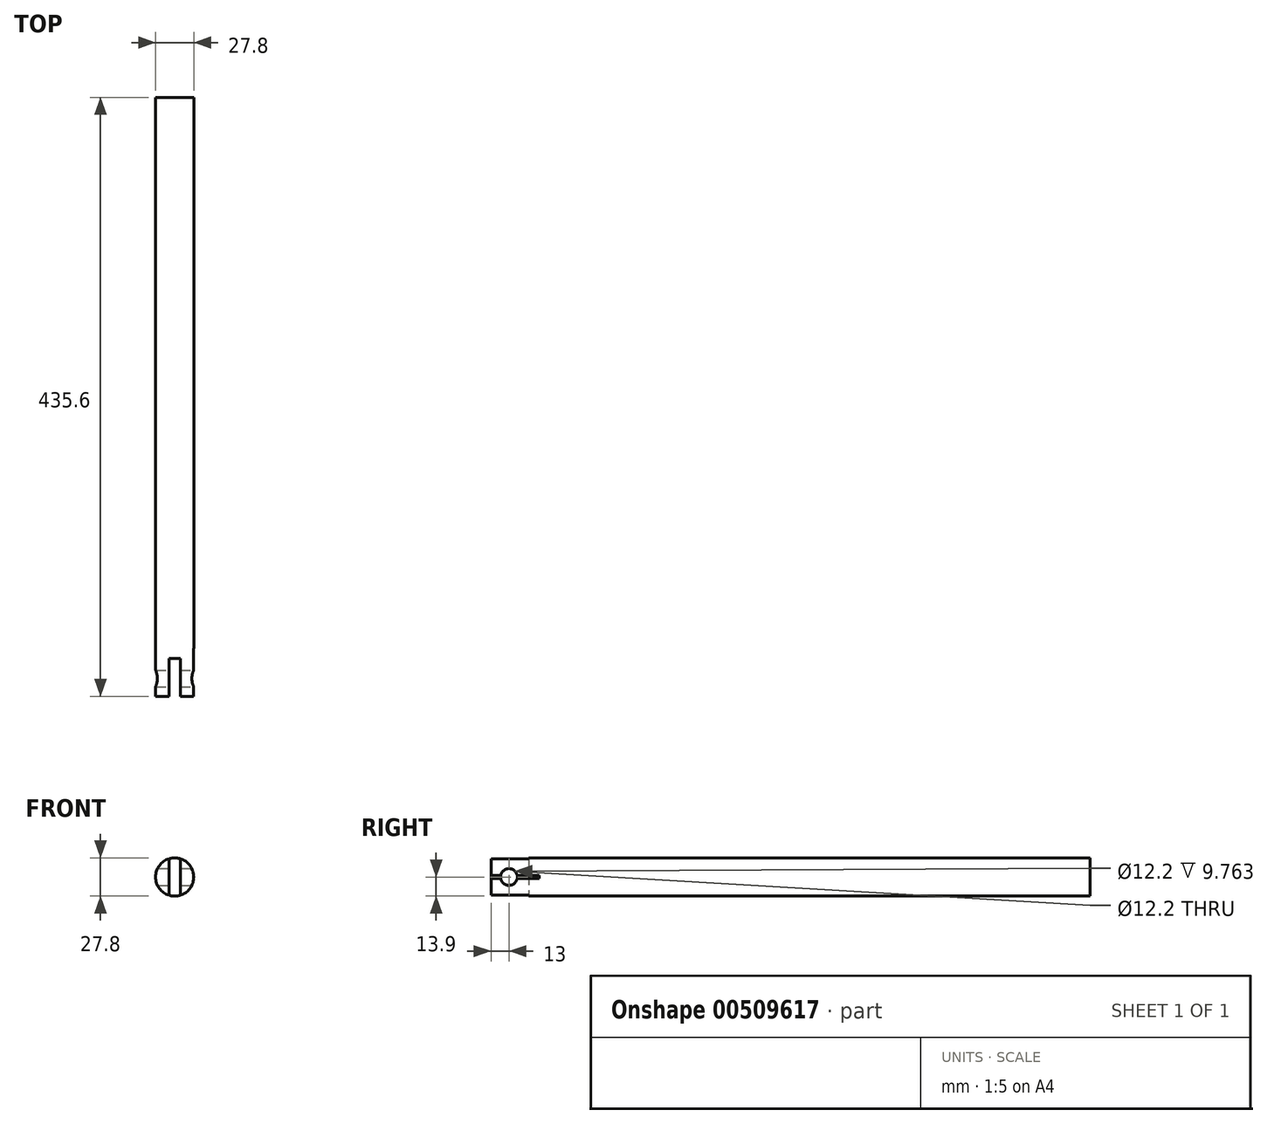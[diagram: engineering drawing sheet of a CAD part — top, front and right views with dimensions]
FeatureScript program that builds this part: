
annotation { "Feature Type Name" : "Feature", "Feature Type Description" : "" }
export const myFeature = defineFeature(function(context is Context, id is Id, definition is map)
    precondition{}
    {
        {
            var Q0;
            Q0=qCreatedBy(makeId("Front.planeOp"),FACE);
            var sketch = newSketch(context, id + "F0", { "sketchPlane" : qUnion([Q0])});
            skCircle(sketch, "E0", {"center": v(0, 0) * mm, "radius": 13.9 * mm});
            skSolve(sketch);
        }
        {
            var Q0;
            Q0=qSketchRegion(id+"F0",true);
            extrude(context, id + "F1", {"entities" : qUnion([Q0]), "endBound" : BoundingType.SYMMETRIC, "depth" : 435.6 * mm});
        }
        {
            var Q0;
            Q0=makeQuery(id+"F1.opExtrude","CAP_FACE",FACE,{"disambiguationData":[OSD([sQuery(id+"F0.wireOp",EDGE,"E0")])],"isStart":false});
            var sketch = newSketch(context, id + "F2", { "sketchPlane" : qUnion([Q0])});
            skLineSegment(sketch, "E1.left", {"start": v(-13.86, 1.02) * mm, "end": v(-13.86, -1.02) * mm});
            skLineSegment(sketch, "E1.right", {"start": v(13.86, 1.02) * mm, "end": v(13.86, -1.02) * mm});
            skPoint(sketch, "E1.middle", {"position": v(0, 0) * mm});
            skSolve(sketch);
        }
        {
            var Q0;
            {var subQ0=sQuery(id+"F2.wireOp",EDGE,"E1.right");Q0=makeQuery(id+"F2.imprint","IMPRINT",FACE,{"disambiguationData":[TD([[makeQuery(id+"F2.imprint","IMPRINT",EDGE,{"derivedFrom":subQ0}),1.0]])]});}
            extrude(context, id + "F3", {"entities" : qUnion([Q0]), "operationType" : NewBodyOperationType.REMOVE, "oppositeDirection" : true, "depth" : 35 * mm});
        }
        {
            var Q0;
            Q0=makeQuery(id+"F3.boolean.opBoolean","COPY",FACE,{"derivedFrom":makeQuery(id+"F3.opExtrude","SWEPT_FACE",FACE,{"disambiguationData":[OSD([sQuery(id+"F2.wireOp",EDGE,"E1.right")])]})});
            var sketch = newSketch(context, id + "F4", { "sketchPlane" : qUnion([Q0])});
            skLineSegment(sketch, "E2", {"start": v(-204.8, 0) * mm, "end": v(-217.8, 0) * mm});
            skPoint(sketch, "E2.startSnap0", {"position": v(-217.8, 0) * mm});
            skSolve(sketch);
        }
        {
            var Q0;
            Q0=sQuery(id+"F4.wireOp",VERTEX,"E2.start");
            var Q1;
            Q1=makeQuery(id+"F1.opExtrude","SWEPT_BODY",BODY,{"disambiguationData":[OSD([sQuery(id+"F0.wireOp",EDGE,"E0")])]});
            hole(context, id + "F5", {"style" : HoleStyle.SIMPLE, "endStyle" : HoleEndStyle.THROUGH, "holeDiameter" : 12.2 * mm, "isTappedThrough" : true, "tappedDepth" : 12 * mm, "tapClearance" : 3, "locations" : qUnion([Q0]), "scope" : qUnion([Q1])});
        }
        {
            var Q0;
            Q0=makeQuery(id+"F1.opExtrude","CAP_FACE",FACE,{"disambiguationData":[OSD([sQuery(id+"F0.wireOp",EDGE,"E0")])],"isStart":false});
            var sketch = newSketch(context, id + "F6", { "sketchPlane" : qUnion([Q0])});
            skLineSegment(sketch, "E3.bottom", {"start": v(-4.1, 39.9) * mm, "end": v(4.1, 39.9) * mm});
            skLineSegment(sketch, "E3.top", {"start": v(-4.1, -39.9) * mm, "end": v(4.1, -39.9) * mm});
            skLineSegment(sketch, "E3.left", {"start": v(-4.1, 39.9) * mm, "end": v(-4.1, -39.9) * mm});
            skLineSegment(sketch, "E3.right", {"start": v(4.1, 39.9) * mm, "end": v(4.1, -39.9) * mm});
            skPoint(sketch, "E3.middle", {"position": v(0, 0) * mm});
            skSolve(sketch);
        }
        {
            var Q0;
            {var subQ0=sQuery(id+"F6.wireOp",EDGE,"E3.left");var subQ1=makeQuery(id+"F1.opExtrude","CAP_EDGE",EDGE,{"disambiguationData":[OSD([sQuery(id+"F0.wireOp",EDGE,"E0")])],"isStart":false});var subQ2=makeQuery(id+"F6.imprint","INTERSECT",VERTEX,{"disambiguationData":[OD(0.0)],"derivedFrom":[subQ1,subQ0]});Q0=makeQuery(id+"F6.imprint","IMPRINT",FACE,{"disambiguationData":[TD([[makeQuery(id+"F6.imprint","IMPRINT",EDGE,{"disambiguationData":[TD([[subQ2,-1.0]])],"derivedFrom":subQ0}),1.0]])]});}
            extrude(context, id + "F7", {"entities" : qUnion([Q0]), "operationType" : NewBodyOperationType.REMOVE, "oppositeDirection" : true, "depth" : 27.5 * mm});
        }
    });
